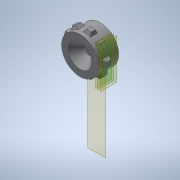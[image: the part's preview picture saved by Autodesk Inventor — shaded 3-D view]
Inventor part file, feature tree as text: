
AUTODESK INVENTOR PART (.ipt)
format: ipt  version: 2020 (Build 240168000, 168)  size: 259,584 bytes
history: native  units: mm
features: other x12, sketch x7, extrude x6, loft x1, pattern_circular x1, chamfer x1, reference x1
ambient origin geometry x8: Origin, YZ Plane, XZ Plane, XY Plane, X Axis, Y Axis, Z Axis, Center Point
bodies: Body1 (feature_tree)
feature tree (29):
  other  "Bryła1"
  other  "Płaszczyzna konstrukcyjna1"
  extrude  "Wyciągnięcie proste1"  Depth=20.0mm
  other  "Płaszczyzna konstrukcyjna2"
  extrude  "Wyciągnięcie proste2"  Depth=50.0mm
  extrude  "Wyciągnięcie proste3"  Depth=20.0mm TaperAngle=0.0deg
  other  "Płaszczyzna konstrukcyjna4"
  other  "Płaszczyzna konstrukcyjna5"
  sketch  "Szkic5"
  other  "Płaszczyzna konstrukcyjna6"
  loft  "Wyciągnięcie złożone1"
  pattern_circular  "Szyk kołowy1"  [2 undecoded]
  extrude  "Wyciągnięcie proste5"  TaperAngle=0.0deg  [1 undecoded]
  sketch  "Szkic10"
  extrude  "Wyciągnięcie proste9"  Depth=3.0mm
  extrude  "Wyciągnięcie proste10"  Depth=12.0mm
  chamfer  "Faza2"  Distance=12.0mm
  sketch  "Szkic1"
  reference  "Odniesienie1"
  sketch  "Szkic3"
  sketch  "Szkic4"
  other  "Płaszczyzna konstrukcyjna3"
  sketch  "Szkic6"
  sketch  "Szkic8"
  other  "<userpath>\Desktop\3d\scanning-robot\Assembly1.iam"
  other  "Assembly1.iam"
  other  "Tower Pro MG90S Micro servo:2"
  other  "Крышка корпуса:1"
  other  "base:1"
note: 3 required parameter values undecoded (feature->parameter linkage not recoverable at this tier; creation-order binding heuristic only, values carry confidence <= 0.55)
